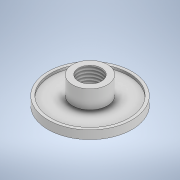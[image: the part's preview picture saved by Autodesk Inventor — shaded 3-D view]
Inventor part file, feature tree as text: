
AUTODESK INVENTOR PART (.ipt)
format: ipt  version: 2022 (Build 260153000, 153)  size: 130,560 bytes
history: native  units: mm
features: extrude x3, sketch x2, other x1, thread x1
ambient origin geometry x8: Origin, YZ Plane, XZ Plane, XY Plane, X Axis, Y Axis, Z Axis, Center Point
bodies: Body1 (feature_tree)
feature tree (7):
  other  "Sólido1"
  sketch  "Boceto1"  dims[d0=69.2mm d1=18.97mm]
  extrude  "Extrusión1"  Depth=18.97mm
  extrude  "Extrusión2"  Depth=21.97mm TaperAngle=0.0deg
  thread  "Rosca1"  [1 undecoded]
  extrude  "Extrusión3"  Depth=21.97mm TaperAngle=0.0deg
  sketch  "Boceto2"  dims[d2=28.9mm d3=21.97mm d4=0.0mm d5=6.95mm d6=0.0mm d7=21.97mm d8=0.0mm d9=64.3mm d10=2.0mm d11=0.0mm]
note: 1 required parameter value undecoded (feature->parameter linkage not recoverable at this tier; creation-order binding heuristic only, values carry confidence <= 0.55)
